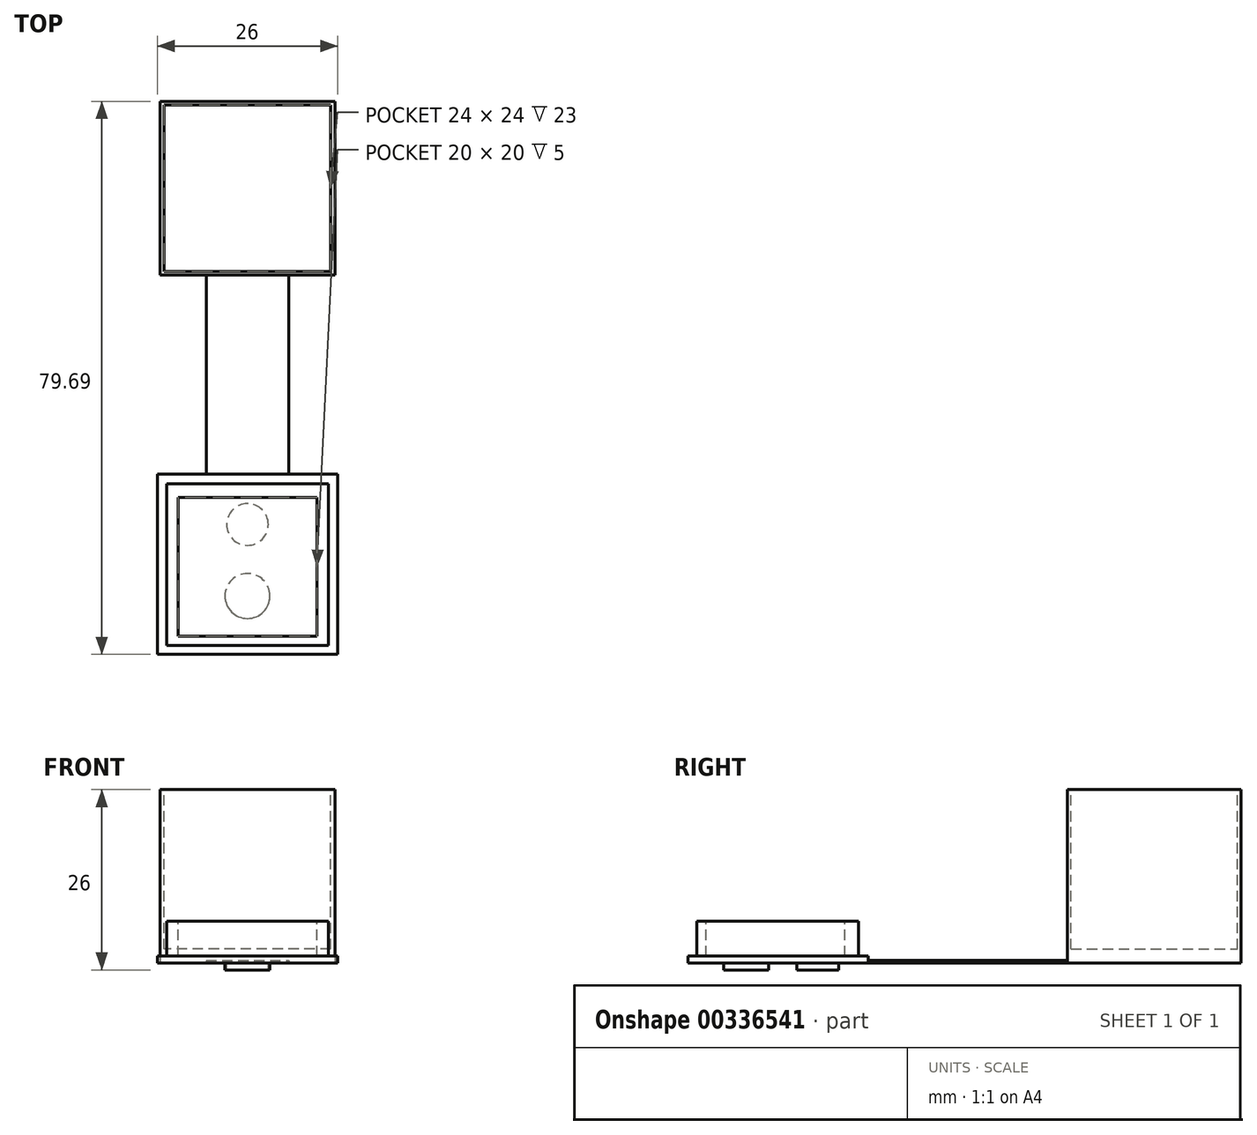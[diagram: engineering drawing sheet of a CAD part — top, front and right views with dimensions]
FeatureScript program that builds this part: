
annotation { "Feature Type Name" : "Feature", "Feature Type Description" : "" }
export const myFeature = defineFeature(function(context is Context, id is Id, definition is map)
    precondition{}
    {
        {
            var Q0;
            Q0=qCreatedBy(makeId("Top.planeOp"),FACE);
            var sketch = newSketch(context, id + "F0", { "sketchPlane" : qUnion([Q0])});
            skLineSegment(sketch, "E0.bottom", {"start": v(12.6, -12.5) * mm, "end": v(-12.6, -12.5) * mm});
            skLineSegment(sketch, "E0.top", {"start": v(12.6, 12.5) * mm, "end": v(-12.6, 12.5) * mm});
            skLineSegment(sketch, "E0.left", {"start": v(12.6, -12.5) * mm, "end": v(12.6, 12.5) * mm});
            skLineSegment(sketch, "E0.right", {"start": v(-12.6, -12.5) * mm, "end": v(-12.6, 12.5) * mm});
            skPoint(sketch, "E0.middle", {"position": v(0, 0) * mm});
            skSolve(sketch);
        }
        {
            var Q0;
            Q0=qCreatedBy(makeId("Top.planeOp"),FACE);
            var sketch = newSketch(context, id + "F1", { "sketchPlane" : qUnion([Q0])});
            skLineSegment(sketch, "E1.bottom", {"start": v(5.94, -46.6) * mm, "end": v(-5.94, -46.6) * mm});
            skPoint(sketch, "E1.middle", {"position": v(0, -17.1) * mm});
            skLineSegment(sketch, "E2", {"start": v(-5.94, -12.45) * mm, "end": v(5.94, -12.45) * mm});
            skLineSegment(sketch, "E3", {"start": v(-5.94, -12.45) * mm, "end": v(-5.94, -46.6) * mm});
            skLineSegment(sketch, "E4", {"start": v(5.94, -12.45) * mm, "end": v(5.94, -46.6) * mm});
            skSolve(sketch);
        }
        {
            var Q0;
            Q0 = qSketchRegion(id + "F0", true);
            extrude(context, id + "F2", {"entities" : qUnion([Q0]), "depth" : 25 * mm});
        }
        {
            var Q0;
            Q0=makeQuery(id+"F2.opExtrude","CAP_FACE",FACE,{"disambiguationData":[OSD([sQuery(id+"F0.wireOp",EDGE,"E0.bottom"),sQuery(id+"F0.wireOp",EDGE,"E0.top"),sQuery(id+"F0.wireOp",EDGE,"E0.left"),sQuery(id+"F0.wireOp",EDGE,"E0.right")])],"isStart":false});
            var sketch = newSketch(context, id + "F3", { "sketchPlane" : qUnion([Q0])});
            skLineSegment(sketch, "E5.bottom", {"start": v(12, -12) * mm, "end": v(-12, -12) * mm});
            skLineSegment(sketch, "E5.top", {"start": v(12, 12) * mm, "end": v(-12, 12) * mm});
            skLineSegment(sketch, "E5.left", {"start": v(12, -12) * mm, "end": v(12, 12) * mm});
            skLineSegment(sketch, "E5.right", {"start": v(-12, -12) * mm, "end": v(-12, 12) * mm});
            skPoint(sketch, "E5.middle", {"position": v(0, 0) * mm});
            skSolve(sketch);
        }
        {
            var Q0;
            Q0 = qSketchRegion(id + "F3", true);
            extrude(context, id + "F4", {"entities" : qUnion([Q0]), "operationType" : NewBodyOperationType.REMOVE, "oppositeDirection" : true, "depth" : 23 * mm});
        }
        {
            var Q0;
            Q0 = qSketchRegion(id + "F1", true);
            extrude(context, id + "F5", {"entities" : qUnion([Q0]), "depth" : 0.4 * mm});
        }
        {
            var Q0;
            Q0=qCreatedBy(makeId("Top.planeOp"),FACE);
            var sketch = newSketch(context, id + "F6", { "sketchPlane" : qUnion([Q0])});
            skLineSegment(sketch, "E6.bottom", {"start": v(13, -67.19) * mm, "end": v(-13, -67.19) * mm});
            skLineSegment(sketch, "E6.top", {"start": v(13, -41.19) * mm, "end": v(-13, -41.19) * mm});
            skLineSegment(sketch, "E6.left", {"start": v(13, -67.19) * mm, "end": v(13, -41.19) * mm});
            skLineSegment(sketch, "E6.right", {"start": v(-13, -67.19) * mm, "end": v(-13, -41.19) * mm});
            skPoint(sketch, "E6.middle", {"position": v(0, -54.19) * mm});
            skSolve(sketch);
        }
        {
            var Q0;
            Q0 = qSketchRegion(id + "F6", true);
            extrude(context, id + "F7", {"entities" : qUnion([Q0]), "operationType" : NewBodyOperationType.ADD, "depth" : 1 * mm});
        }
        {
            var Q0;
            Q0=makeQuery(id+"F7.opExtrude","CAP_FACE",FACE,{"disambiguationData":[OSD([sQuery(id+"F6.wireOp",EDGE,"E6.bottom"),sQuery(id+"F6.wireOp",EDGE,"E6.top"),sQuery(id+"F6.wireOp",EDGE,"E6.left"),sQuery(id+"F6.wireOp",EDGE,"E6.right")])],"isStart":false});
            var sketch = newSketch(context, id + "F8", { "sketchPlane" : qUnion([Q0])});
            skLineSegment(sketch, "E7.bottom", {"start": v(11.65, -65.93) * mm, "end": v(-11.65, -65.93) * mm});
            skLineSegment(sketch, "E7.top", {"start": v(11.65, -42.63) * mm, "end": v(-11.65, -42.63) * mm});
            skLineSegment(sketch, "E7.left", {"start": v(11.65, -65.93) * mm, "end": v(11.65, -42.63) * mm});
            skLineSegment(sketch, "E7.right", {"start": v(-11.65, -65.93) * mm, "end": v(-11.65, -42.63) * mm});
            skPoint(sketch, "E7.middle", {"position": v(0, -54.28) * mm});
            skSolve(sketch);
        }
        {
            var Q0;
            Q0 = qSketchRegion(id + "F8", true);
            extrude(context, id + "F9", {"entities" : qUnion([Q0]), "operationType" : NewBodyOperationType.ADD, "depth" : 5 * mm});
        }
        {
            var Q0;
            Q0=makeQuery(id+"F9.opExtrude","CAP_FACE",FACE,{"disambiguationData":[OSD([sQuery(id+"F8.wireOp",EDGE,"E7.bottom"),sQuery(id+"F8.wireOp",EDGE,"E7.top"),sQuery(id+"F8.wireOp",EDGE,"E7.left"),sQuery(id+"F8.wireOp",EDGE,"E7.right")])],"isStart":false});
            var sketch = newSketch(context, id + "F10", { "sketchPlane" : qUnion([Q0])});
            skLineSegment(sketch, "E8.bottom", {"start": v(10, -64.58) * mm, "end": v(-10, -64.58) * mm});
            skLineSegment(sketch, "E8.top", {"start": v(10, -44.58) * mm, "end": v(-10, -44.58) * mm});
            skLineSegment(sketch, "E8.left", {"start": v(10, -64.58) * mm, "end": v(10, -44.58) * mm});
            skLineSegment(sketch, "E8.right", {"start": v(-10, -64.58) * mm, "end": v(-10, -44.58) * mm});
            skPoint(sketch, "E8.middle", {"position": v(0, -54.58) * mm});
            skSolve(sketch);
        }
        {
            var Q0;
            Q0 = qSketchRegion(id + "F10", true);
            extrude(context, id + "F11", {"entities" : qUnion([Q0]), "operationType" : NewBodyOperationType.REMOVE, "oppositeDirection" : true, "depth" : 5 * mm});
        }
        {
            var Q0;
            Q0=makeQuery(id+"F7.boolean.opBoolean","MERGE",FACE,{"derivedFrom":[makeQuery(id+"F5.opExtrude","CAP_FACE",FACE,{"disambiguationData":[OSD([sQuery(id+"F1.wireOp",EDGE,"E1.bottom"),sQuery(id+"F1.wireOp",EDGE,"E2"),sQuery(id+"F1.wireOp",EDGE,"E3"),sQuery(id+"F1.wireOp",EDGE,"E4")])],"isStart":true}),makeQuery(id+"F7.opExtrude","CAP_FACE",FACE,{"disambiguationData":[OSD([sQuery(id+"F6.wireOp",EDGE,"E6.bottom"),sQuery(id+"F6.wireOp",EDGE,"E6.top"),sQuery(id+"F6.wireOp",EDGE,"E6.left"),sQuery(id+"F6.wireOp",EDGE,"E6.right")])],"isStart":true})]});
            var sketch = newSketch(context, id + "F12", { "sketchPlane" : qUnion([Q0])});
            skCircle(sketch, "E9", {"center": v(0, 48.48) * mm, "radius": 3 * mm});
            skCircle(sketch, "E10", {"center": v(0, 58.78) * mm, "radius": 3.24 * mm});
            skSolve(sketch);
        }
        {
            var Q0;
            Q0 = qSketchRegion(id + "F12", true);
            extrude(context, id + "F13", {"entities" : qUnion([Q0]), "operationType" : NewBodyOperationType.ADD, "depth" : 1 * mm, "offsetDistance" : 25.4 * mm});
        }
    });
